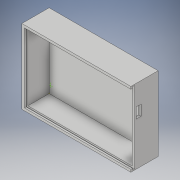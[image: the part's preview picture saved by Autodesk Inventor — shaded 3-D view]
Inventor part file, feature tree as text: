
AUTODESK INVENTOR PART (.ipt)
format: ipt  version: 2018.3 (Build 223284000, 284)  size: 158,208 bytes
history: native  units: in
note: dims shown in document units (in); Inventor stores cm internally (conversion verified against a paired STEP export)
features: sketch x9, extrude x5, other x3, shell x1, split x1, delete_face x1
ambient origin geometry x8: Origin, YZ Plane, XZ Plane, XY Plane, X Axis, Y Axis, Z Axis, Center Point
bodies: Solid1 (feature_tree)
feature tree (20):
  extrude  "Extrusion1"  Depth=2.2047in
  shell  "Shell1"  Thickness=0.7874in
  split  "Split1"
  delete_face  "Delete Face1"
  sketch  "Sketch3"  dims[d6=0.3346in d7=0.7874in d8=0.394in d9=0.0in d10=0.0in]
  sketch  "Sketch4"  dims[d11=0.05in d12=0.04in d13=0.0584in d14=0.05in d15=0.12in d16=0.08in d17=0.009in d18=0.03in d19=0.481in d20=0.3436in]
  other  "Snap Fit1"
  other  "Snap Fit2"
  extrude  "Extrusion2"  Depth=0.1575in
  extrude  "Extrusion3"  Depth=0.7874in TaperAngle=0.0deg
  extrude  "Extrusion4"  Depth=2.3in
  sketch  "Sketch1"  dims[d0=3.3071in d1=2.2047in d2=0.7874in d3=0.0in]
  sketch  "Sketch2"  dims[d4=0.0787in d5=0.1575in]
  other  "Srf1"
  sketch  "Sketch5"  dims[d21=0.05in d22=0.04in d23=0.0584in d24=0.05in d25=0.12in d26=0.08in d27=0.009in d28=0.03in d29=0.481in d30=0.3436in d31=2.3in]
  sketch  "Sketch6"  dims[d32=90.0deg d33=0.06in]
  sketch  "Sketch7"  dims[d34=0.031in]
  sketch  "Sketch8"  dims[d35=3.4375in d36=0.0in]
  sketch  "Sketch9"  dims[d37=0.11in d38=0.0in d39=0.11in d40=0.0in]
  extrude  "ExtrusionSrf1"  Depth=0.06in
